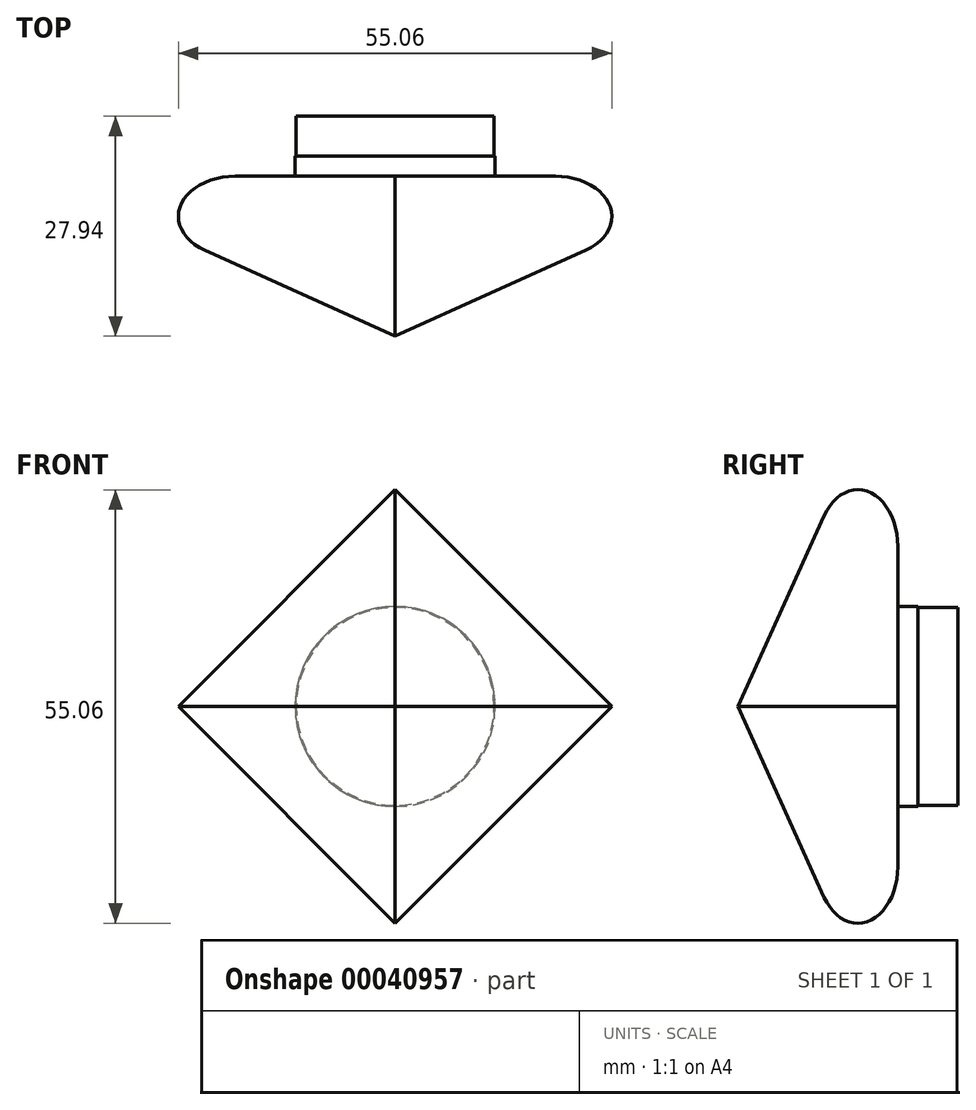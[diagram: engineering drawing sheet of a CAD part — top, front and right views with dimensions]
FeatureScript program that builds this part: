
annotation { "Feature Type Name" : "Feature", "Feature Type Description" : "" }
export const myFeature = defineFeature(function(context is Context, id is Id, definition is map)
    precondition{}
    {
        {
            var Q0;
            Q0=qCreatedBy(makeId("Front.planeOp"),FACE);
            var sketch = newSketch(context, id + "F0", { "sketchPlane" : qUnion([Q0])});
            skCircle(sketch, "E0.cCircle", {"center": v(0, 0) * mm, "radius": 31.75 * mm, "construction": true});
            skLineSegment(sketch, "E0.0", {"start": v(0, -44.9) * mm, "end": v(-44.9, 0) * mm});
            skLineSegment(sketch, "E0.1", {"start": v(-44.9, 0) * mm, "end": v(0, 44.9) * mm});
            skLineSegment(sketch, "E0.2", {"start": v(0, 44.9) * mm, "end": v(44.9, 0) * mm});
            skLineSegment(sketch, "E0.3", {"start": v(44.9, 0) * mm, "end": v(0, -44.9) * mm});
            skPoint(sketch, "E0.0.midPoint", {"position": v(-22.45, -22.45) * mm});
            skSolve(sketch);
        }
        {
            var Q0;
            Q0=qCreatedBy(makeId("Top.planeOp"),FACE);
            var sketch = newSketch(context, id + "F1", { "sketchPlane" : qUnion([Q0])});
            skPoint(sketch, "E1", {"position": v(0, -20.32) * mm});
            skSolve(sketch);
        }
        {
            var Q0;
            Q0=makeQuery(id+"F0.imprint","IMPRINT",FACE,{"disambiguationData":[TD([[makeQuery(id+"F0.imprint","IMPRINT",EDGE,{"derivedFrom":sQuery(id+"F0.wireOp",EDGE,"E0.0")}),-1.0]])]});
            var Q1;
            Q1=sQuery(id+"F1.wireOp",VERTEX,"E1");
            var Q2;
            Q2=sQuery(id+"F0.wireOp",EDGE,"E0.1");
            var Q3;
            Q3=sQuery(id+"F1.wireOp",VERTEX,"E1");
            loft(context, id + "F2", {"sheetProfilesArray" : [{ "sheetProfileEntities" : qUnion([Q0]) }, { "sheetProfileEntities" : qUnion([Q1]) }], "wireProfilesArray" : [{ "wireProfileEntities" : qUnion([Q2]) }, { "wireProfileEntities" : qUnion([Q3]) }]});
        }
        {
            var Q0;
            Q0=makeQuery(id+"F2.opLoft","CAP_FACE",FACE,{"disambiguationData":[OSD([makeQuery(id+"F0.imprint","IMPRINT",FACE,{"disambiguationData":[TD([[makeQuery(id+"F0.imprint","IMPRINT",EDGE,{"derivedFrom":sQuery(id+"F0.wireOp",EDGE,"E0.0")}),-1.0]])]})])],"isStart":true});
            fillet(context, id + "F3", {"entities" : qUnion([Q0]), "radius" : 5.08 * mm, "tangentPropagation" : true, "allowEdgeOverflow" : false});
        }
        {
            var Q0;
            Q0=makeQuery(id+"F2.opLoft","CAP_FACE",FACE,{"disambiguationData":[OSD([makeQuery(id+"F0.imprint","IMPRINT",FACE,{"disambiguationData":[TD([[makeQuery(id+"F0.imprint","IMPRINT",EDGE,{"derivedFrom":sQuery(id+"F0.wireOp",EDGE,"E0.0")}),-1.0]])]})])],"isStart":true});
            var sketch = newSketch(context, id + "F4", { "sketchPlane" : qUnion([Q0])});
            skCircle(sketch, "E2", {"center": v(0, 0) * mm, "radius": 12.7 * mm});
            skSolve(sketch);
        }
        {
            var Q0;
            Q0=makeQuery(id+"F4.imprint","IMPRINT",FACE,{"disambiguationData":[TD([[makeQuery(id+"F4.imprint","IMPRINT",EDGE,{"derivedFrom":sQuery(id+"F4.wireOp",EDGE,"E2")}),1.0]])]});
            extrude(context, id + "F5", {"entities" : qUnion([Q0]), "operationType" : NewBodyOperationType.ADD, "depth" : 2.54 * mm});
        }
        {
            var Q0;
            Q0=makeQuery(id+"F5.opExtrude","CAP_FACE",FACE,{"disambiguationData":[OSD([sQuery(id+"F4.wireOp",EDGE,"E2")])],"isStart":false});
            var sketch = newSketch(context, id + "F6", { "sketchPlane" : qUnion([Q0])});
            skCircle(sketch, "E3", {"center": v(0, 0) * mm, "radius": 12.57 * mm});
            skSolve(sketch);
        }
        {
            var Q0;
            Q0=qSketchRegion(id+"F6",true);
            extrude(context, id + "F7", {"entities" : qUnion([Q0]), "operationType" : NewBodyOperationType.ADD, "depth" : 5.08 * mm});
        }
    });
